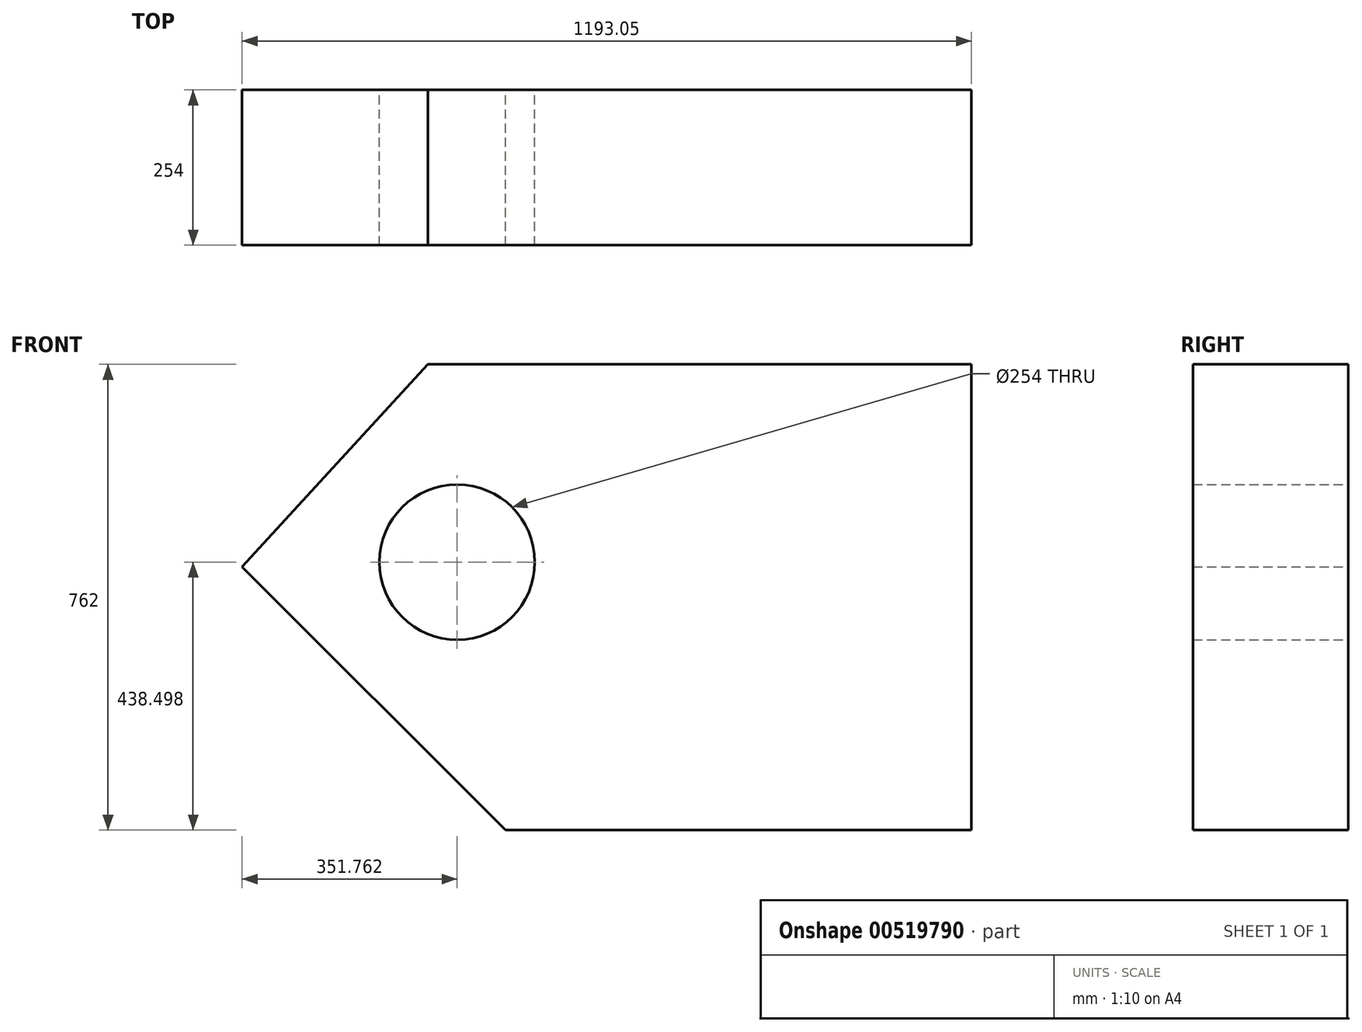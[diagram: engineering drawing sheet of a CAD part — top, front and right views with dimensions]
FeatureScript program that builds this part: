
annotation { "Feature Type Name" : "Feature", "Feature Type Description" : "" }
export const myFeature = defineFeature(function(context is Context, id is Id, definition is map)
    precondition{}
    {
        {
            var Q0;
            Q0=qCreatedBy(makeId("Front.planeOp"),FACE);
            var sketch = newSketch(context, id + "F0", { "sketchPlane" : qUnion([Q0])});
            skLineSegment(sketch, "E0", {"start": v(0, 0) * mm, "end": v(889, 0) * mm});
            skLineSegment(sketch, "E1", {"start": v(889, 0) * mm, "end": v(889, -762) * mm});
            skLineSegment(sketch, "E2", {"start": v(889, -762) * mm, "end": v(127, -762) * mm});
            skLineSegment(sketch, "E3", {"start": v(127, -762) * mm, "end": v(-304.05, -330.95) * mm});
            skLineSegment(sketch, "E4", {"start": v(0, 0) * mm, "end": v(-304.05, -330.95) * mm});
            skCircle(sketch, "E5", {"center": v(47.71, -323.5) * mm, "radius": 127 * mm});
            skSolve(sketch);
        }
        {
            var Q0;
            Q0=makeQuery(id+"F0.imprint","IMPRINT",FACE,{"disambiguationData":[TD([[makeQuery(id+"F0.imprint","IMPRINT",EDGE,{"derivedFrom":sQuery(id+"F0.wireOp",EDGE,"E0")}),-1.0]])]});
            extrude(context, id + "F1", {"entities" : qUnion([Q0]), "depth" : 254 * mm, "offsetDistance" : 25.4 * mm});
        }
    });
